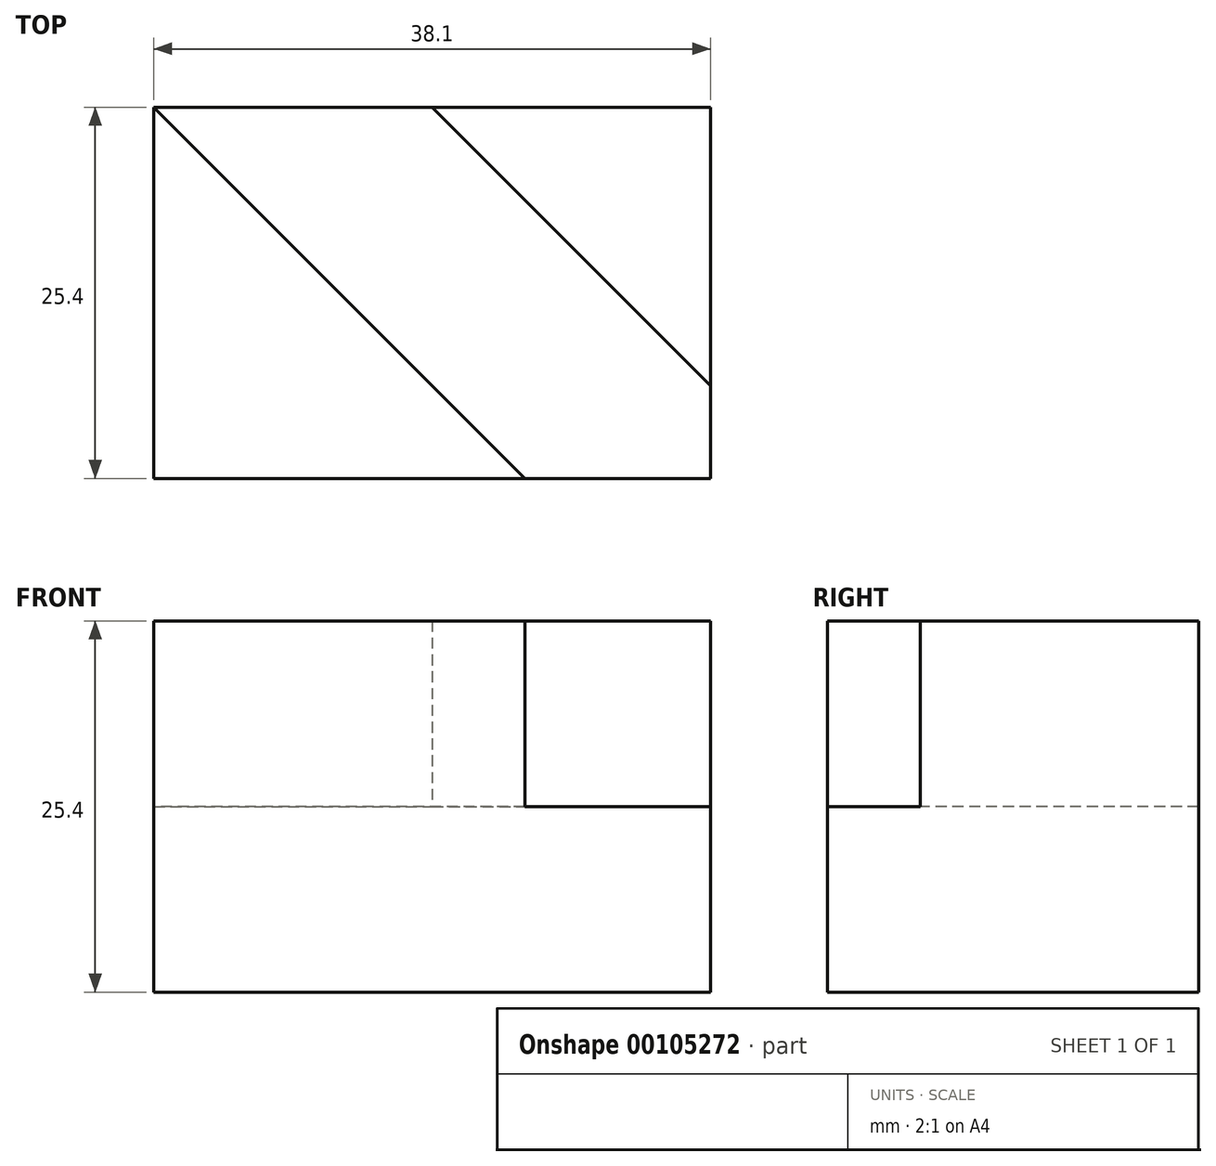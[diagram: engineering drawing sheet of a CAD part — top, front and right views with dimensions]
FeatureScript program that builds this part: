
annotation { "Feature Type Name" : "Feature", "Feature Type Description" : "" }
export const myFeature = defineFeature(function(context is Context, id is Id, definition is map)
    precondition{}
    {
        {
            var Q0;
            Q0=qCreatedBy(makeId("Front.planeOp"),FACE);
            var sketch = newSketch(context, id + "F0", { "sketchPlane" : qUnion([Q0])});
            skLineSegment(sketch, "E0.bottom", {"start": v(0, 0) * mm, "end": v(38.1, 0) * mm});
            skLineSegment(sketch, "E0.top", {"start": v(0, 12.7) * mm, "end": v(38.1, 12.7) * mm});
            skLineSegment(sketch, "E0.left", {"start": v(0, 0) * mm, "end": v(0, 12.7) * mm});
            skLineSegment(sketch, "E0.right", {"start": v(38.1, 0) * mm, "end": v(38.1, 12.7) * mm});
            skSolve(sketch);
        }
        {
            var Q0;
            Q0=makeQuery(id+"F0.imprint","IMPRINT",FACE,{"disambiguationData":[TD([[makeQuery(id+"F0.imprint","IMPRINT",EDGE,{"derivedFrom":sQuery(id+"F0.wireOp",EDGE,"E0.bottom")}),1.0]])]});
            extrude(context, id + "F1", {"entities" : qUnion([Q0]), "depth" : 25.4 * mm});
        }
        {
            var Q0;
            Q0=makeQuery(id+"F1.opExtrude","SWEPT_FACE",FACE,{"disambiguationData":[OSD([sQuery(id+"F0.wireOp",EDGE,"E0.top")])]});
            var sketch = newSketch(context, id + "F2", { "sketchPlane" : qUnion([Q0])});
            skLineSegment(sketch, "E1", {"start": v(0, 0) * mm, "end": v(0, -25.4) * mm});
            skLineSegment(sketch, "E2", {"start": v(0, -25.4) * mm, "end": v(25.4, -25.4) * mm});
            skLineSegment(sketch, "E3", {"start": v(25.4, -25.4) * mm, "end": v(0, 0) * mm});
            skLineSegment(sketch, "E4", {"start": v(38.1, 0) * mm, "end": v(19.05, 0) * mm});
            skLineSegment(sketch, "E5", {"start": v(19.05, 0) * mm, "end": v(38.1, -19.05) * mm});
            skLineSegment(sketch, "E6", {"start": v(38.1, -19.05) * mm, "end": v(38.1, 0) * mm});
            skSolve(sketch);
        }
        {
            var Q0;
            Q0=makeQuery(id+"F2.imprint","IMPRINT",FACE,{"disambiguationData":[TD([[makeQuery(id+"F2.imprint","IMPRINT",EDGE,{"derivedFrom":sQuery(id+"F2.wireOp",EDGE,"E1")}),-1.0]])]});
            var Q1;
            Q1=makeQuery(id+"F2.imprint","IMPRINT",FACE,{"disambiguationData":[TD([[makeQuery(id+"F2.imprint","IMPRINT",EDGE,{"derivedFrom":sQuery(id+"F2.wireOp",EDGE,"E4")}),-1.0]])]});
            extrude(context, id + "F3", {"entities" : qUnion([Q0, Q1]), "operationType" : NewBodyOperationType.ADD, "depth" : 12.7 * mm});
        }
    });
